# Revit family: Турникет тумбовый PERCo_TTD-08A
name_source: partatom
category: Mechanical Equipment
units: mm (PartAtom-declared; Revit-internal decimal feet)

## family parameters
Always vertical = No
Classification = None
Cut with Voids When Loaded = No
Part Type = Normal
Room Calculation Point = No
Round Connector Dimension = Use Diameter
Shared = No
Work Plane-Based = No

## types (1)
- TTD-08A
    Built-in reader = not provided
    Card capture reader capacity = not provided
    Current = 6 A
    Dimensions = 1166×750×1016 mm
    Electrical connection = 220 V
    Frame = Stainless steel
    Full name = TTD-08A Electromechanical Box Tripod Turnstile with Automatic Anti-Panic Barrier Arms
    IP Code = IP54
    Lid_insert = Plastic black
    Manufacturer = PERCo
    Material = Housing ─ high-quality stainless steel with ABS plastic inserts. Barrier arms ─ stainless steel.
    Maximum dimensions of ACS controller = max. 135×90×30 mm
    Maximum dimensions of installed readers = max.  250×130×35 mm
    Name = TTD-08A Box tripod turnstile
    Number = 1
    Operating temperature = from -20°C to +50°C, without shelter
    Passageway width = 560 mm
    Plank = Stainless steel
    Plank base = Black
    Plank length = 567 mm  [stored 1.86024 ft]
    Rated power = 72 W
    Throughput rate = 30 persons/min
    URL = https://www.perco.com
    Unit of measurement = pcs
    Voltage = 12 V
    Weight = max. 70 kg

note: [stored X ft] marks values corroborated as IEEE doubles in the binary element streams (Revit-internal decimal feet)
